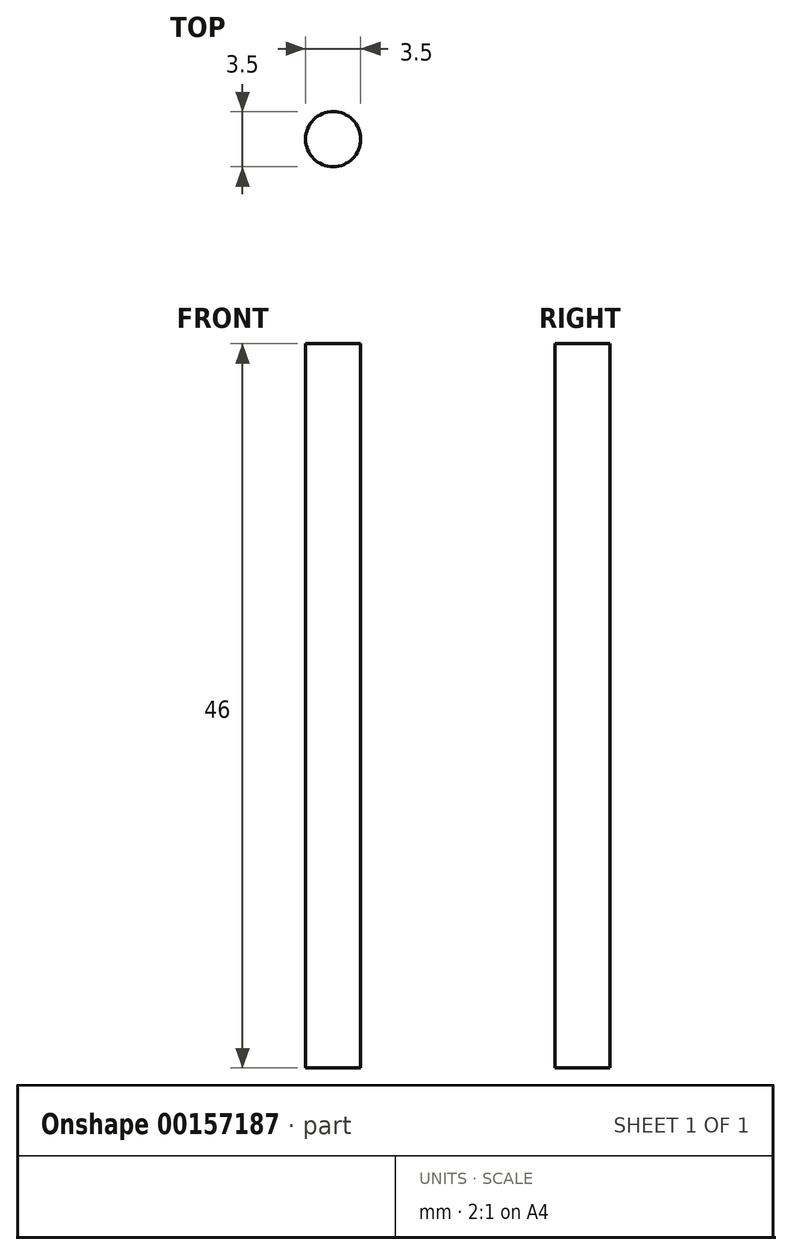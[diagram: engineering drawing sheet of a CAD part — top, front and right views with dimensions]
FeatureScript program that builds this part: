
annotation { "Feature Type Name" : "Feature", "Feature Type Description" : "" }
export const myFeature = defineFeature(function(context is Context, id is Id, definition is map)
    precondition{}
    {
        {
            var Q0;
            Q0=qCreatedBy(makeId("Top.planeOp"),FACE);
            var sketch = newSketch(context, id + "F0", { "sketchPlane" : qUnion([Q0])});
            skCircle(sketch, "E0", {"center": v(0, 0) * mm, "radius": 1.75 * mm});
            skSolve(sketch);
        }
        {
            var Q0;
            Q0 = qSketchRegion(id + "F0", true);
            extrude(context, id + "F1", {"entities" : qUnion([Q0]), "depth" : 46 * mm});
        }
    });
